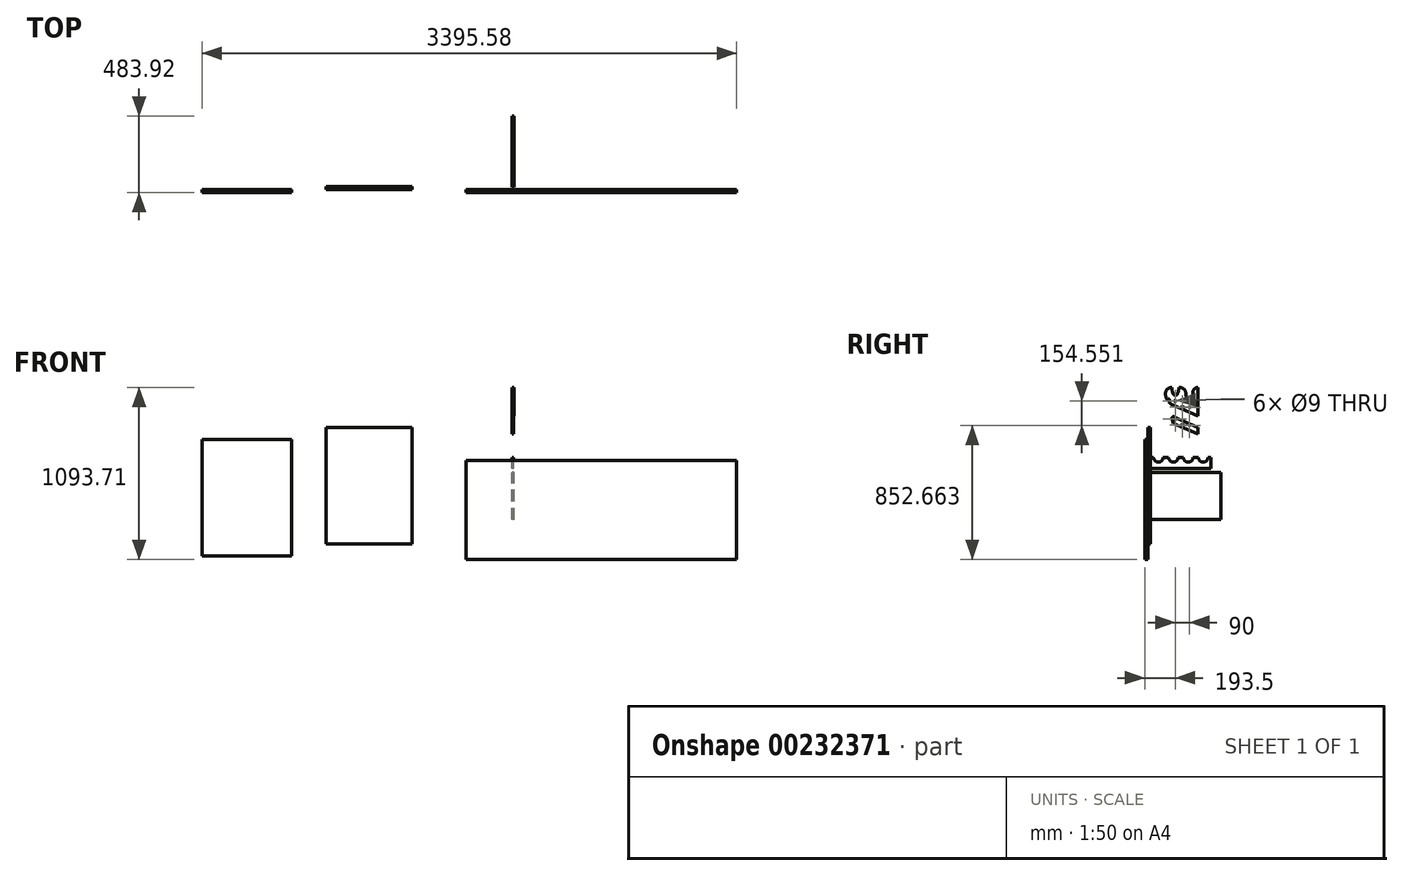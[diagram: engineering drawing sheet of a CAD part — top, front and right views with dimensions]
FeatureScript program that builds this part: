
annotation { "Feature Type Name" : "Feature", "Feature Type Description" : "" }
export const myFeature = defineFeature(function(context is Context, id is Id, definition is map)
    precondition{}
    {
        {
            var Q0;
            Q0=qCreatedBy(makeId("Right.planeOp"),FACE);
            var sketch = newSketch(context, id + "F0", { "sketchPlane" : qUnion([Q0])});
            skLineSegment(sketch, "E0.bottom", {"start": v(0, 0) * mm, "end": v(385, 0) * mm});
            skLineSegment(sketch, "E0.top", {"start": v(0, 70) * mm, "end": v(20, 70) * mm});
            skLineSegment(sketch, "E0.left", {"start": v(0, 0) * mm, "end": v(0, 70) * mm});
            skLineSegment(sketch, "E0.right", {"start": v(385, 0) * mm, "end": v(385, 70) * mm});
            skArc(sketch, "E1", {"start": v(20, 70) * mm, "mid": v(50, 40) * mm, "end": v(80, 70) * mm});
            skLineSegment(sketch, "E2.trimOffspring", {"start": v(80, 70) * mm, "end": v(115, 70) * mm});
            skArc(sketch, "E3.1.0.0", {"start": v(115, 70) * mm, "mid": v(145, 40) * mm, "end": v(175, 70) * mm});
            skArc(sketch, "E3.2.0.0", {"start": v(210, 70) * mm, "mid": v(240, 40) * mm, "end": v(270, 70) * mm});
            skLineSegment(sketch, "E3.direction1", {"start": v(20, 70) * mm, "end": v(115, 70) * mm, "construction": true});
            skLineSegment(sketch, "E4.trimOffspring", {"start": v(175, 70) * mm, "end": v(210, 70) * mm});
            skLineSegment(sketch, "E5.trimOffspring", {"start": v(270, 70) * mm, "end": v(305, 70) * mm});
            skArc(sketch, "E6.0.3.0", {"start": v(305, 70) * mm, "mid": v(335, 40) * mm, "end": v(365, 70) * mm});
            skLineSegment(sketch, "E7.trimOffspring", {"start": v(365, 70) * mm, "end": v(385, 70) * mm});
            skSolve(sketch);
        }
        {
            var Q0;
            Q0=makeQuery(id+"F0.imprint","IMPRINT",FACE,{"disambiguationData":[TD([[makeQuery(id+"F0.imprint","IMPRINT",EDGE,{"derivedFrom":sQuery(id+"F0.wireOp",EDGE,"E0.bottom")}),1.0]])]});
            extrude(context, id + "F1", {"entities" : qUnion([Q0]), "depth" : 10 * mm});
        }
        {
            var Q0;
            Q0=qCreatedBy(makeId("Right.planeOp"),FACE);
            var sketch = newSketch(context, id + "F2", { "sketchPlane" : qUnion([Q0])});
            skEllipse(sketch, "E8", {"center": v(247.5, 475) * mm, "majorRadius": 50 * mm, "minorRadius": 20 * mm, "majorAxis": v(0, 1), "construction": true});
            skLineSegment(sketch, "E9.direction2", {"start": v(247.5, 475) * mm, "end": v(247.5, 515) * mm, "construction": true});
            skLineSegment(sketch, "E10", {"start": v(300, 475) * mm, "end": v(300, 225) * mm, "construction": true});
            skArc(sketch, "E11", {"start": v(233.82, 433.85) * mm, "mid": v(247.5, 425) * mm, "end": v(261.18, 433.85) * mm});
            skArc(sketch, "E12", {"start": v(261.18, 433.85) * mm, "mid": v(267.77, 453.96) * mm, "end": v(270, 475) * mm});
            skArc(sketch, "E13.MirrorCS", {"start": v(233.82, 433.85) * mm, "mid": v(227.23, 453.96) * mm, "end": v(225, 475) * mm});
            skArc(sketch, "E14", {"start": v(143.82, 473.85) * mm, "mid": v(157.5, 465) * mm, "end": v(171.18, 473.85) * mm});
            skArc(sketch, "E15", {"start": v(171.18, 473.85) * mm, "mid": v(177.77, 493.96) * mm, "end": v(180, 515) * mm});
            skArc(sketch, "E16.MirrorCS", {"start": v(143.82, 473.85) * mm, "mid": v(137.23, 493.96) * mm, "end": v(135, 515) * mm});
            skLineSegment(sketch, "E17", {"start": v(270, 475) * mm, "end": v(270, 485) * mm});
            skArc(sketch, "E18", {"start": v(300, 515) * mm, "mid": v(278.79, 506.21) * mm, "end": v(270, 485) * mm});
            skLineSegment(sketch, "E19", {"start": v(180, 515) * mm, "end": v(185, 515) * mm});
            skArc(sketch, "E20", {"start": v(225, 475) * mm, "mid": v(213.28, 503.28) * mm, "end": v(185, 515) * mm});
            skLineSegment(sketch, "E21", {"start": v(180, 515) * mm, "end": v(180, 545.58) * mm, "construction": true});
            skLineSegment(sketch, "E22", {"start": v(157.5, 480) * mm, "end": v(157.5, 507.06) * mm, "construction": true});
            skArc(sketch, "E23", {"start": v(135, 515) * mm, "mid": v(106.72, 503.28) * mm, "end": v(95, 475) * mm});
            skLineSegment(sketch, "E24", {"start": v(135, 515) * mm, "end": v(225, 475) * mm, "construction": true});
            skLineSegment(sketch, "E25", {"start": v(110, 471.4) * mm, "end": v(300, 386.95) * mm, "construction": true});
            skLineSegment(sketch, "E26", {"start": v(300, 515) * mm, "end": v(300, 332.22) * mm});
            skLineSegment(sketch, "E27", {"start": v(300, 332.22) * mm, "end": v(142.06, 402.54) * mm});
            skArc(sketch, "E28", {"start": v(95, 475) * mm, "mid": v(107.8, 431.8) * mm, "end": v(142.06, 402.54) * mm});
            skLineSegment(sketch, "E29", {"start": v(142.06, 402.54) * mm, "end": v(142.06, 402.54) * mm});
            skSolve(sketch);
        }
        {
            var Q0;
            Q0=makeQuery(id+"F2.imprint","IMPRINT",FACE,{"disambiguationData":[TD([[makeQuery(id+"F2.imprint","IMPRINT",EDGE,{"derivedFrom":sQuery(id+"F2.wireOp",EDGE,"E11")}),-1.0]])]});
            extrude(context, id + "F3", {"entities" : qUnion([Q0]), "depth" : 12 * mm});
        }
        {
            var Q0;
            Q0=qCreatedBy(makeId("Right.planeOp"),FACE);
            var sketch = newSketch(context, id + "F4", { "sketchPlane" : qUnion([Q0])});
            skLineSegment(sketch, "E30", {"start": v(300, 261.52) * mm, "end": v(300, 217.74) * mm});
            skLineSegment(sketch, "E31", {"start": v(300, 217.74) * mm, "end": v(145, 286.75) * mm});
            skLineSegment(sketch, "E32", {"start": v(145, 286.75) * mm, "end": v(136.19, 316.4) * mm});
            skLineSegment(sketch, "E33", {"start": v(149.84, 328.38) * mm, "end": v(300, 261.52) * mm});
            skPoint(sketch, "E34.visualSharp", {"position": v(130, 337.21) * mm});
            skArc(sketch, "E34.filletArc", {"start": v(149.84, 328.38) * mm, "mid": v(139.18, 326.76) * mm, "end": v(136.19, 316.4) * mm});
            skLineSegment(sketch, "E35", {"start": v(247.5, 482.42) * mm, "end": v(247.5, 241.16) * mm, "construction": true});
            skLineSegment(sketch, "E36", {"start": v(157.5, 522) * mm, "end": v(157.5, 314.02) * mm, "construction": true});
            skLineSegment(sketch, "E37", {"start": v(157.5, 314.02) * mm, "end": v(247.5, 273.95) * mm, "construction": true});
            skLineSegment(sketch, "E38.0", {"start": v(155.47, 298.5) * mm, "end": v(245.47, 258.44) * mm, "construction": true});
            skLineSegment(sketch, "E39.0", {"start": v(202.5, 482.42) * mm, "end": v(202.5, 277.57) * mm, "construction": true});
            skCircle(sketch, "E40", {"center": v(157.5, 314.02) * mm, "radius": 4.5 * mm});
            skCircle(sketch, "E41", {"center": v(202.5, 277.57) * mm, "radius": 4.5 * mm});
            skCircle(sketch, "E42", {"center": v(247.5, 273.95) * mm, "radius": 4.5 * mm});
            skSolve(sketch);
        }
        {
            var Q0;
            Q0=makeQuery(id+"F4.imprint","IMPRINT",FACE,{"disambiguationData":[TD([[makeQuery(id+"F4.imprint","IMPRINT",EDGE,{"derivedFrom":sQuery(id+"F4.wireOp",EDGE,"E30")}),-1.0]])]});
            extrude(context, id + "F5", {"entities" : qUnion([Q0]), "depth" : 10 * mm});
        }
        {
            var Q0;
            Q0=makeQuery(id+"F3.opExtrude","CAP_FACE",FACE,{"disambiguationData":[OSD([sQuery(id+"F2.wireOp",EDGE,"E11"),sQuery(id+"F2.wireOp",EDGE,"E12"),sQuery(id+"F2.wireOp",EDGE,"E13.MirrorCS"),sQuery(id+"F2.wireOp",EDGE,"E14"),sQuery(id+"F2.wireOp",EDGE,"E15"),sQuery(id+"F2.wireOp",EDGE,"E16.MirrorCS"),sQuery(id+"F2.wireOp",EDGE,"E17"),sQuery(id+"F2.wireOp",EDGE,"E18"),sQuery(id+"F2.wireOp",EDGE,"E19"),sQuery(id+"F2.wireOp",EDGE,"E20"),sQuery(id+"F2.wireOp",EDGE,"E23"),sQuery(id+"F2.wireOp",EDGE,"E26"),sQuery(id+"F2.wireOp",EDGE,"E27"),sQuery(id+"F2.wireOp",EDGE,"E28")])],"isStart":false});
            var sketch = newSketch(context, id + "F6", { "sketchPlane" : qUnion([Q0])});
            skLineSegment(sketch, "E43", {"start": v(300, 332.22) * mm, "end": v(145, 401.23) * mm, "construction": true});
            skPoint(sketch, "E44.visualSharp", {"position": v(265.97, 400.38) * mm});
            skCircle(sketch, "E45", {"center": v(157.5, 428.5) * mm, "radius": 4.5 * mm});
            skCircle(sketch, "E46", {"center": v(202.5, 392.05) * mm, "radius": 4.5 * mm});
            skCircle(sketch, "E47", {"center": v(247.5, 388.43) * mm, "radius": 4.5 * mm});
            skSolve(sketch);
        }
        {
            var Q0;
            Q0 = qSketchRegion(id + "F6", true);
            extrude(context, id + "F7", {"entities" : qUnion([Q0]), "operationType" : NewBodyOperationType.REMOVE, "endBound" : BoundingType.THROUGH_ALL, "oppositeDirection" : true, "depth" : 25 * mm});
        }
        {
            var Q0;
            Q0=qCreatedBy(makeId("Front.planeOp"),FACE);
            var sketch = newSketch(context, id + "F8", { "sketchPlane" : qUnion([Q0])});
            skLineSegment(sketch, "E48.bottom", {"start": v(-635.47, -479.32) * mm, "end": v(-1180.47, -479.32) * mm});
            skLineSegment(sketch, "E48.top", {"start": v(-635.47, 260.68) * mm, "end": v(-1180.47, 260.68) * mm});
            skLineSegment(sketch, "E48.left", {"start": v(-635.47, -479.32) * mm, "end": v(-635.47, 260.68) * mm});
            skLineSegment(sketch, "E48.right", {"start": v(-1180.47, -479.32) * mm, "end": v(-1180.47, 260.68) * mm});
            skSolve(sketch);
        }
        {
            var Q0;
            Q0=makeQuery(id+"F8.imprint","IMPRINT",FACE,{"disambiguationData":[TD([[makeQuery(id+"F8.imprint","IMPRINT",EDGE,{"derivedFrom":sQuery(id+"F8.wireOp",EDGE,"E48.bottom")}),-1.0]])]});
            extrude(context, id + "F9", {"entities" : qUnion([Q0]), "depth" : 18 * mm});
        }
        {
            var Q0;
            Q0=makeQuery(id+"F9.opExtrude","CAP_FACE",FACE,{"disambiguationData":[OSD([sQuery(id+"F8.wireOp",EDGE,"E48.bottom"),sQuery(id+"F8.wireOp",EDGE,"E48.top"),sQuery(id+"F8.wireOp",EDGE,"E48.left"),sQuery(id+"F8.wireOp",EDGE,"E48.right")])],"isStart":false});
            var sketch = newSketch(context, id + "F10", { "sketchPlane" : qUnion([Q0])});
            skLineSegment(sketch, "E49.bottom", {"start": v(-1968.24, -556.24) * mm, "end": v(-1398.24, -556.24) * mm});
            skLineSegment(sketch, "E49.top", {"start": v(-1968.24, 183.76) * mm, "end": v(-1398.24, 183.76) * mm});
            skLineSegment(sketch, "E49.left", {"start": v(-1968.24, -556.24) * mm, "end": v(-1968.24, 183.76) * mm});
            skLineSegment(sketch, "E49.right", {"start": v(-1398.24, -556.24) * mm, "end": v(-1398.24, 183.76) * mm});
            skSolve(sketch);
        }
        {
            var Q0;
            Q0=makeQuery(id+"F10.imprint","IMPRINT",FACE,{"disambiguationData":[TD([[makeQuery(id+"F10.imprint","IMPRINT",EDGE,{"derivedFrom":sQuery(id+"F10.wireOp",EDGE,"E49.bottom")}),1.0]])]});
            extrude(context, id + "F11", {"entities" : qUnion([Q0]), "depth" : 18 * mm});
        }
        {
            var Q0;
            Q0=makeQuery(id+"F9.opExtrude","CAP_FACE",FACE,{"disambiguationData":[OSD([sQuery(id+"F8.wireOp",EDGE,"E48.bottom"),sQuery(id+"F8.wireOp",EDGE,"E48.top"),sQuery(id+"F8.wireOp",EDGE,"E48.left"),sQuery(id+"F8.wireOp",EDGE,"E48.right")])],"isStart":false});
            var sketch = newSketch(context, id + "F12", { "sketchPlane" : qUnion([Q0])});
            skLineSegment(sketch, "E50.bottom", {"start": v(-292.66, -578.71) * mm, "end": v(1427.34, -578.71) * mm});
            skLineSegment(sketch, "E50.top", {"start": v(-292.66, 51.29) * mm, "end": v(1427.34, 51.29) * mm});
            skLineSegment(sketch, "E50.left", {"start": v(-292.66, -578.71) * mm, "end": v(-292.66, 51.29) * mm});
            skLineSegment(sketch, "E50.right", {"start": v(1427.34, -578.71) * mm, "end": v(1427.34, 51.29) * mm});
            skSolve(sketch);
        }
        {
            var Q0;
            Q0=makeQuery(id+"F12.imprint","IMPRINT",FACE,{"disambiguationData":[TD([[makeQuery(id+"F12.imprint","IMPRINT",EDGE,{"derivedFrom":sQuery(id+"F12.wireOp",EDGE,"E50.bottom")}),1.0]])]});
            extrude(context, id + "F13", {"entities" : qUnion([Q0]), "depth" : 18 * mm});
        }
        {
            var Q0;
            Q0=qCreatedBy(makeId("Right.planeOp"),FACE);
            var sketch = newSketch(context, id + "F14", { "sketchPlane" : qUnion([Q0])});
            skLineSegment(sketch, "E51.bottom", {"start": v(-2.08, -324.8) * mm, "end": v(447.92, -324.8) * mm});
            skLineSegment(sketch, "E51.top", {"start": v(-2.08, -24.8) * mm, "end": v(447.92, -24.8) * mm});
            skLineSegment(sketch, "E51.left", {"start": v(-2.08, -324.8) * mm, "end": v(-2.08, -24.8) * mm});
            skLineSegment(sketch, "E51.right", {"start": v(447.92, -324.8) * mm, "end": v(447.92, -24.8) * mm});
            skSolve(sketch);
        }
        {
            var Q0;
            Q0=makeQuery(id+"F14.imprint","IMPRINT",FACE,{"disambiguationData":[TD([[makeQuery(id+"F14.imprint","IMPRINT",EDGE,{"derivedFrom":sQuery(id+"F14.wireOp",EDGE,"E51.bottom")}),1.0]])]});
            extrude(context, id + "F15", {"entities" : qUnion([Q0]), "depth" : 12 * mm});
        }
        {
            var Q0;
            Q0=makeQuery(id+"F3.opExtrude","CAP_FACE",FACE,{"disambiguationData":[OSD([sQuery(id+"F2.wireOp",EDGE,"E11"),sQuery(id+"F2.wireOp",EDGE,"E12"),sQuery(id+"F2.wireOp",EDGE,"E13.MirrorCS"),sQuery(id+"F2.wireOp",EDGE,"E14"),sQuery(id+"F2.wireOp",EDGE,"E15"),sQuery(id+"F2.wireOp",EDGE,"E16.MirrorCS"),sQuery(id+"F2.wireOp",EDGE,"E17"),sQuery(id+"F2.wireOp",EDGE,"E18"),sQuery(id+"F2.wireOp",EDGE,"E19"),sQuery(id+"F2.wireOp",EDGE,"E20"),sQuery(id+"F2.wireOp",EDGE,"E23"),sQuery(id+"F2.wireOp",EDGE,"E26"),sQuery(id+"F2.wireOp",EDGE,"E27"),sQuery(id+"F2.wireOp",EDGE,"E28")])],"isStart":false});
            var sketch = newSketch(context, id + "F16", { "sketchPlane" : qUnion([Q0])});
            skLineSegment(sketch, "E52", {"start": v(120.26, 406.96) * mm, "end": v(120.26, 436.8) * mm});
            skLineSegment(sketch, "E53", {"start": v(112.45, 440.95) * mm, "end": v(90.55, 426.1) * mm});
            skLineSegment(sketch, "E54", {"start": v(90.55, 426.1) * mm, "end": v(120.26, 406.96) * mm});
            skPoint(sketch, "E55.visualSharp", {"position": v(120.26, 446.24) * mm});
            skArc(sketch, "E55.filletArc", {"start": v(120.26, 436.8) * mm, "mid": v(117.6, 441.22) * mm, "end": v(112.45, 440.95) * mm});
            skSolve(sketch);
        }
        {
            var Q0;
            {var subQ0=sQuery(id+"F16.wireOp",EDGE,"E54");Q0=makeQuery(id+"F16.imprint","IMPRINT",FACE,{"disambiguationData":[TD([[makeQuery(id+"F16.imprint","IMPRINT",EDGE,{"derivedFrom":subQ0}),1.0]])]});}
            var Q1;
            {var subQ0=sQuery(id+"F16.wireOp",EDGE,"E55.filletArc");Q1=makeQuery(id+"F16.imprint","IMPRINT",FACE,{"disambiguationData":[TD([[makeQuery(id+"F16.imprint","IMPRINT",EDGE,{"derivedFrom":subQ0}),1.0]])]});}
            extrude(context, id + "F17", {"entities" : qUnion([Q0, Q1]), "operationType" : NewBodyOperationType.REMOVE, "oppositeDirection" : true, "depth" : 25 * mm});
        }
        {
            var Q0;
            Q0=makeQuery(id+"F17.boolean.opBoolean","INTERSECT",EDGE,{"derivedFrom":[makeQuery(id+"F3.opExtrude","SWEPT_FACE",FACE,{"disambiguationData":[OSD([sQuery(id+"F2.wireOp",EDGE,"E28")])]}),makeQuery(id+"F17.opExtrude","SWEPT_FACE",FACE,{"disambiguationData":[OSD([sQuery(id+"F16.wireOp",EDGE,"E53")])]})]});
            fillet(context, id + "F18", {"entities" : qUnion([Q0]), "radius" : 5 * mm, "tangentPropagation" : true, "allowEdgeOverflow" : false});
        }
    });
